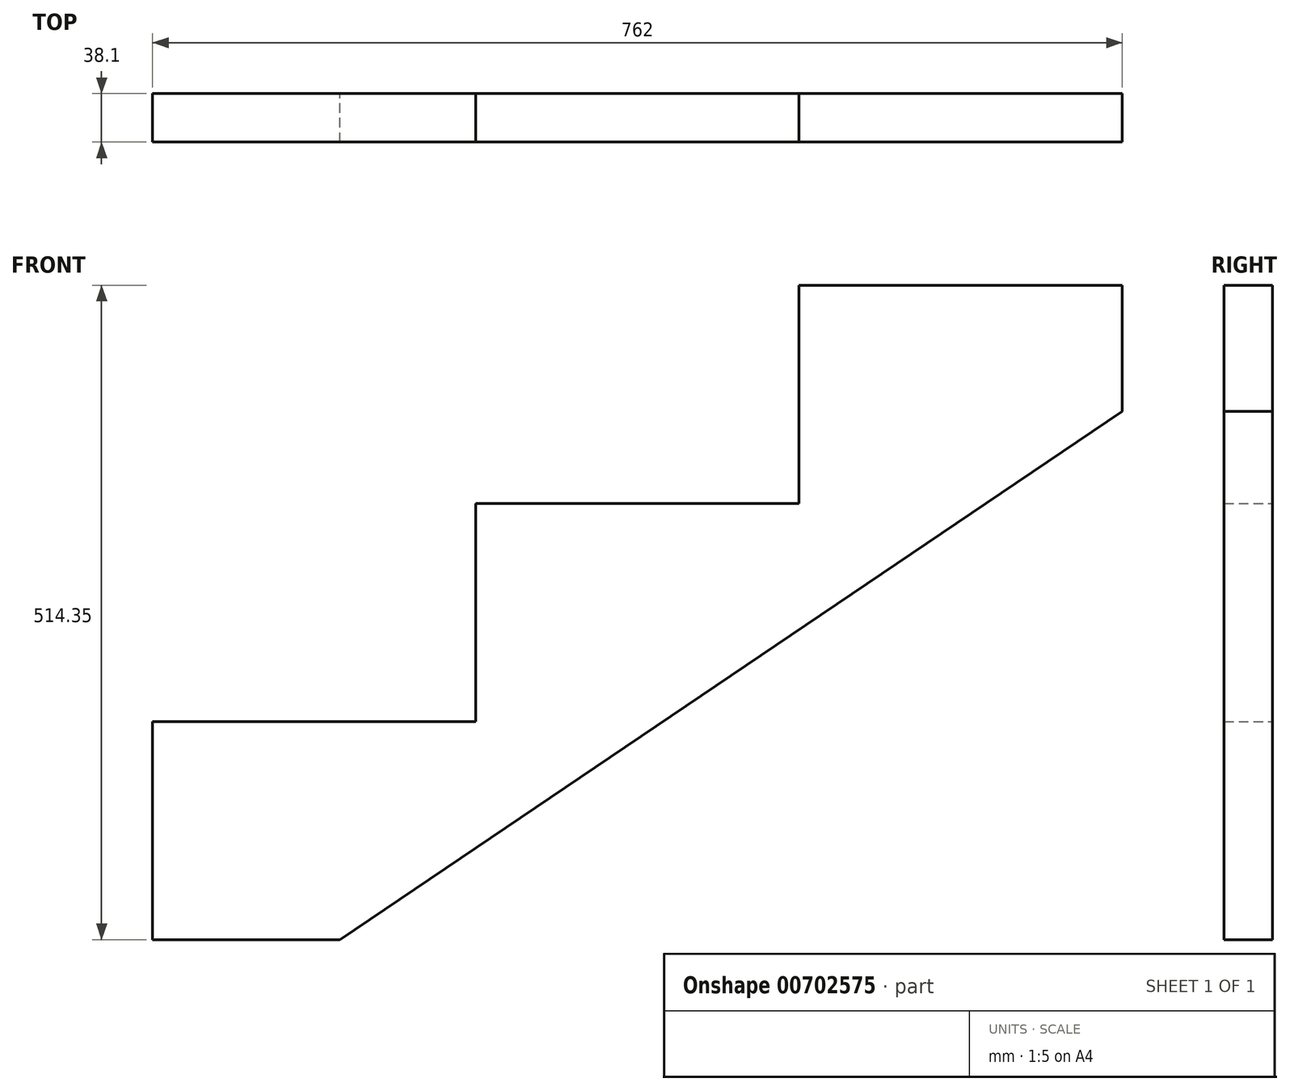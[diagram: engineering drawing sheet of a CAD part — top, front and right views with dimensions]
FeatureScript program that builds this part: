
annotation { "Feature Type Name" : "Feature", "Feature Type Description" : "" }
export const myFeature = defineFeature(function(context is Context, id is Id, definition is map)
    precondition{}
    {
        {
            var Q0;
            Q0=qCreatedBy(makeId("Front.planeOp"),FACE);
            var sketch = newSketch(context, id + "F0", { "sketchPlane" : qUnion([Q0])});
            skLineSegment(sketch, "E0", {"start": v(0, 0) * mm, "end": v(0, 171.45) * mm});
            skLineSegment(sketch, "E1", {"start": v(0, 171.45) * mm, "end": v(254, 171.45) * mm});
            skLineSegment(sketch, "E2", {"start": v(254, 171.45) * mm, "end": v(254, 342.9) * mm});
            skLineSegment(sketch, "E3", {"start": v(254, 342.9) * mm, "end": v(508, 342.9) * mm});
            skLineSegment(sketch, "E4", {"start": v(508, 342.9) * mm, "end": v(508, 514.35) * mm});
            skLineSegment(sketch, "E5", {"start": v(508, 514.35) * mm, "end": v(762, 514.35) * mm});
            skLineSegment(sketch, "E6", {"start": v(254, 342.9) * mm, "end": v(415.64, 181.26) * mm});
            skLineSegment(sketch, "E7", {"start": v(508, 514.35) * mm, "end": v(669.64, 352.7) * mm});
            skLineSegment(sketch, "E8", {"start": v(0, 171.45) * mm, "end": v(161.64, 9.8) * mm});
            skLineSegment(sketch, "E9", {"start": v(762, 415.04) * mm, "end": v(147.14, 0) * mm});
            skLineSegment(sketch, "E10", {"start": v(762, 514.35) * mm, "end": v(762, 415.04) * mm});
            skLineSegment(sketch, "E11", {"start": v(0, 0) * mm, "end": v(147.14, 0) * mm});
            skSolve(sketch);
        }
        {
            var Q0;
            Q0 = qSketchRegion(id + "F0", true);
            extrude(context, id + "F1", {"entities" : qUnion([Q0]), "depth" : 38.1 * mm, "offsetDistance" : 25.4 * mm});
        }
    });
